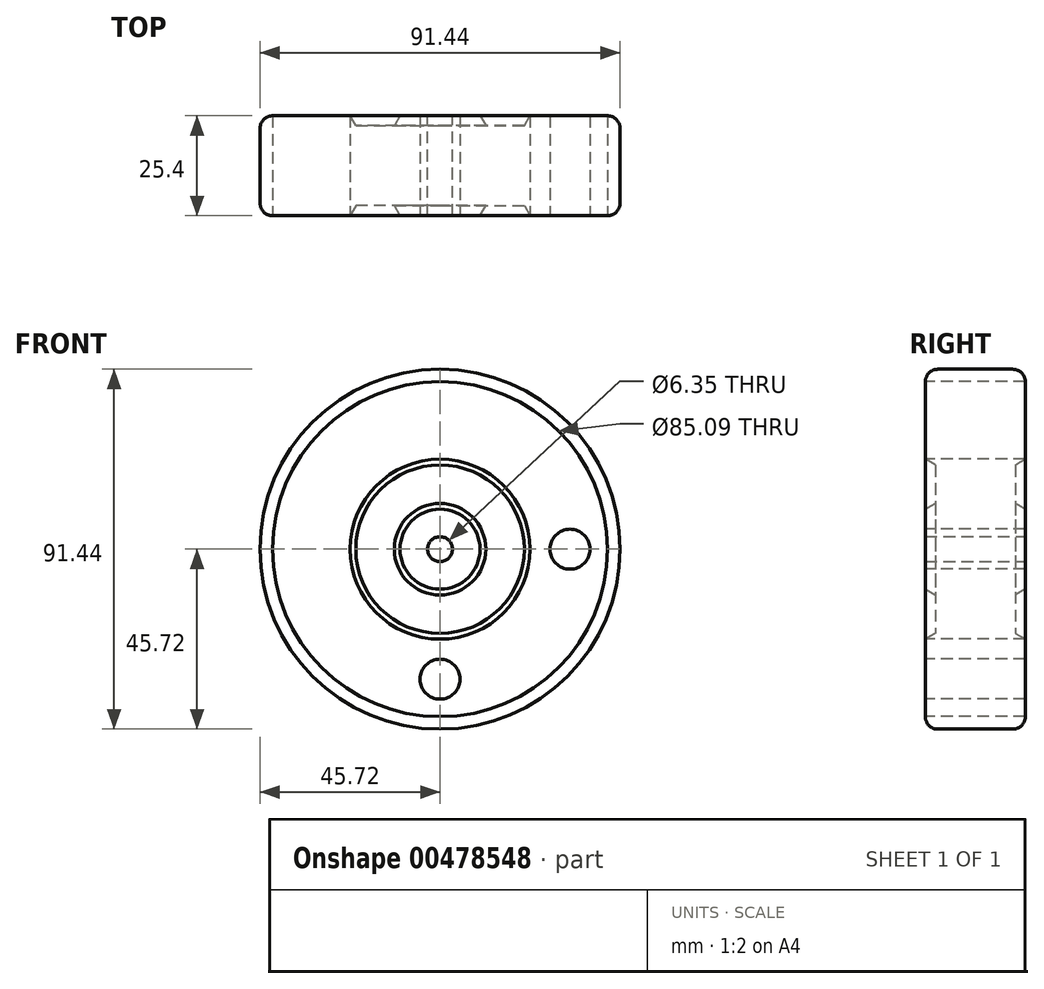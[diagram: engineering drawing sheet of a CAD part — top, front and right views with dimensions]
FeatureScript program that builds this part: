
annotation { "Feature Type Name" : "Feature", "Feature Type Description" : "" }
export const myFeature = defineFeature(function(context is Context, id is Id, definition is map)
    precondition{}
    {
        {
            var Q0;
            Q0=qCreatedBy(makeId("Right.planeOp"),FACE);
            var sketch = newSketch(context, id + "F0", { "sketchPlane" : qUnion([Q0])});
            skLineSegment(sketch, "E0", {"start": v(0, 0) * mm, "end": v(45.88, 0) * mm, "construction": true});
            skLineSegment(sketch, "E1", {"start": v(12.7, 3.18) * mm, "end": v(12.7, 10.16) * mm});
            skLineSegment(sketch, "E2", {"start": v(12.7, 10.16) * mm, "end": v(10.16, 11.63) * mm});
            skLineSegment(sketch, "E3", {"start": v(10.16, 11.63) * mm, "end": v(10.16, 21.4) * mm});
            skLineSegment(sketch, "E4", {"start": v(10.16, 21.4) * mm, "end": v(12.7, 22.86) * mm});
            skLineSegment(sketch, "E5", {"start": v(12.7, 22.86) * mm, "end": v(12.7, 42.55) * mm});
            skLineSegment(sketch, "E6.MirrorCS", {"start": v(-10.16, 21.4) * mm, "end": v(-12.7, 22.86) * mm});
            skLineSegment(sketch, "E7.MirrorCS", {"start": v(-12.7, 10.16) * mm, "end": v(-10.16, 11.63) * mm});
            skLineSegment(sketch, "E8.MirrorCS", {"start": v(-10.16, 11.63) * mm, "end": v(-10.16, 21.4) * mm});
            skLineSegment(sketch, "E9.MirrorCS", {"start": v(0, 0) * mm, "end": v(-45.88, 0) * mm, "construction": true});
            skLineSegment(sketch, "E10.MirrorCS", {"start": v(-12.7, 3.18) * mm, "end": v(-12.7, 10.16) * mm});
            skLineSegment(sketch, "E11.MirrorCS", {"start": v(-12.7, 22.86) * mm, "end": v(-12.7, 42.55) * mm});
            skLineSegment(sketch, "E12", {"start": v(-9.52, 45.72) * mm, "end": v(9.52, 45.72) * mm});
            skPoint(sketch, "E13.visualSharp", {"position": v(-12.7, 45.72) * mm});
            skArc(sketch, "E13.filletArc", {"start": v(-9.52, 45.72) * mm, "mid": v(-11.77, 44.8) * mm, "end": v(-12.7, 42.55) * mm});
            skPoint(sketch, "E14.visualSharp", {"position": v(12.7, 45.72) * mm});
            skArc(sketch, "E14.filletArc", {"start": v(12.7, 42.55) * mm, "mid": v(11.77, 44.8) * mm, "end": v(9.52, 45.72) * mm});
            skLineSegment(sketch, "E15", {"start": v(-12.7, 3.18) * mm, "end": v(12.7, 3.18) * mm});
            skSolve(sketch);
        }
        {
            var Q0;
            Q0=makeQuery(id+"F0.imprint","IMPRINT",FACE,{"disambiguationData":[TD([[makeQuery(id+"F0.imprint","IMPRINT",EDGE,{"derivedFrom":sQuery(id+"F0.wireOp",EDGE,"E1")}),1.0]])]});
            var Q1;
            Q1=sQuery(id+"F0.wireOp",EDGE,"E9.MirrorCS");
            revolve(context, id + "F1", {"entities" : qUnion([Q0]), "axis" : qUnion([Q1]), "revolveType" : RevolveType.FULL});
        }
        {
            var Q0;
            Q0=makeQuery(id+"F1.opRevolve","SWEPT_BODY",BODY,{"disambiguationData":[OSD([sQuery(id+"F0.wireOp",EDGE,"E1"),sQuery(id+"F0.wireOp",EDGE,"E2"),sQuery(id+"F0.wireOp",EDGE,"E3"),sQuery(id+"F0.wireOp",EDGE,"E4"),sQuery(id+"F0.wireOp",EDGE,"E5"),sQuery(id+"F0.wireOp",EDGE,"E6.MirrorCS"),sQuery(id+"F0.wireOp",EDGE,"E7.MirrorCS"),sQuery(id+"F0.wireOp",EDGE,"E8.MirrorCS"),sQuery(id+"F0.wireOp",EDGE,"E10.MirrorCS"),sQuery(id+"F0.wireOp",EDGE,"E11.MirrorCS"),sQuery(id+"F0.wireOp",EDGE,"E12"),sQuery(id+"F0.wireOp",EDGE,"E13.filletArc"),sQuery(id+"F0.wireOp",EDGE,"E14.filletArc"),sQuery(id+"F0.wireOp",EDGE,"E15")])]});
            transform(context, id + "F2", {"entities" : qUnion([Q0]), "transformType" : TransformType.TRANSLATION_3D, "dx" : 0 * mm, "dy" : 0 * mm, "dz" : 0 * mm, "makeCopy" : true});
        }
        {
            var Q0;
            Q0=makeQuery(id+"F1.opRevolve","SWEPT_BODY",BODY,{"disambiguationData":[OSD([sQuery(id+"F0.wireOp",EDGE,"E1"),sQuery(id+"F0.wireOp",EDGE,"E2"),sQuery(id+"F0.wireOp",EDGE,"E3"),sQuery(id+"F0.wireOp",EDGE,"E4"),sQuery(id+"F0.wireOp",EDGE,"E5"),sQuery(id+"F0.wireOp",EDGE,"E6.MirrorCS"),sQuery(id+"F0.wireOp",EDGE,"E7.MirrorCS"),sQuery(id+"F0.wireOp",EDGE,"E8.MirrorCS"),sQuery(id+"F0.wireOp",EDGE,"E10.MirrorCS"),sQuery(id+"F0.wireOp",EDGE,"E11.MirrorCS"),sQuery(id+"F0.wireOp",EDGE,"E12"),sQuery(id+"F0.wireOp",EDGE,"E13.filletArc"),sQuery(id+"F0.wireOp",EDGE,"E14.filletArc"),sQuery(id+"F0.wireOp",EDGE,"E15")])]});
            deleteBodies(context, id + "F3", {"entities" : qUnion([Q0])});
        }
        {
            var Q0;
            Q0=makeQuery(id+"F2.opPattern","COPY",FACE,{"derivedFrom":makeQuery(id+"F1.opRevolve","SWEPT_FACE",FACE,{"disambiguationData":[OSD([sQuery(id+"F0.wireOp",EDGE,"E11.MirrorCS")])]}),"instanceName":"1"});
            var sketch = newSketch(context, id + "F4", { "sketchPlane" : qUnion([Q0])});
            skCircle(sketch, "E16", {"center": v(0, 0) * mm, "radius": 33.02 * mm});
            skCircle(sketch, "E17", {"center": v(0, 33.02) * mm, "radius": 5.08 * mm});
            skCircle(sketch, "E18", {"center": v(33.02, 0) * mm, "radius": 5.08 * mm});
            skCircle(sketch, "E19", {"center": v(0, -33.02) * mm, "radius": 5.08 * mm});
            skCircle(sketch, "E20", {"center": v(-33.02, 0) * mm, "radius": 5.08 * mm});
            skSolve(sketch);
        }
        {
            var Q0;
            {var subQ0=sQuery(id+"F4.wireOp",EDGE,"E17");var subQ1=sQuery(id+"F4.wireOp",EDGE,"E16");var subQ2=makeQuery(id+"F4.imprint","INTERSECT",VERTEX,{"disambiguationData":[OD(0.0)],"derivedFrom":[subQ1,subQ0]});Q0=makeQuery(id+"F4.imprint","IMPRINT",FACE,{"disambiguationData":[TD([[makeQuery(id+"F4.imprint","IMPRINT",EDGE,{"disambiguationData":[TD([[subQ2,-1.0]])],"derivedFrom":subQ1}),1.0]])]});}
            var Q1;
            {var subQ0=sQuery(id+"F4.wireOp",EDGE,"E17");var subQ1=sQuery(id+"F4.wireOp",EDGE,"E16");var subQ2=makeQuery(id+"F4.imprint","INTERSECT",VERTEX,{"disambiguationData":[OD(0.0)],"derivedFrom":[subQ1,subQ0]});Q1=makeQuery(id+"F4.imprint","IMPRINT",FACE,{"disambiguationData":[TD([[makeQuery(id+"F4.imprint","IMPRINT",EDGE,{"disambiguationData":[TD([[subQ2,-1.0]])],"derivedFrom":subQ1}),-1.0]])]});}
            var Q2;
            {var subQ0=sQuery(id+"F4.wireOp",EDGE,"E18");var subQ1=sQuery(id+"F4.wireOp",EDGE,"E16");var subQ2=makeQuery(id+"F4.imprint","INTERSECT",VERTEX,{"disambiguationData":[OD(0.0)],"derivedFrom":[subQ1,subQ0]});Q2=makeQuery(id+"F4.imprint","IMPRINT",FACE,{"disambiguationData":[TD([[makeQuery(id+"F4.imprint","IMPRINT",EDGE,{"disambiguationData":[TD([[subQ2,1.0]])],"derivedFrom":subQ1}),1.0]])]});}
            var Q3;
            {var subQ0=sQuery(id+"F4.wireOp",EDGE,"E18");var subQ1=sQuery(id+"F4.wireOp",EDGE,"E16");var subQ2=makeQuery(id+"F4.imprint","INTERSECT",VERTEX,{"disambiguationData":[OD(0.0)],"derivedFrom":[subQ1,subQ0]});Q3=makeQuery(id+"F4.imprint","IMPRINT",FACE,{"disambiguationData":[TD([[makeQuery(id+"F4.imprint","IMPRINT",EDGE,{"disambiguationData":[TD([[subQ2,1.0]])],"derivedFrom":subQ1}),-1.0]])]});}
            var Q4;
            {var subQ0=sQuery(id+"F4.wireOp",EDGE,"E19");var subQ1=sQuery(id+"F4.wireOp",EDGE,"E16");var subQ2=makeQuery(id+"F4.imprint","INTERSECT",VERTEX,{"disambiguationData":[OD(0.0)],"derivedFrom":[subQ1,subQ0]});Q4=makeQuery(id+"F4.imprint","IMPRINT",FACE,{"disambiguationData":[TD([[makeQuery(id+"F4.imprint","IMPRINT",EDGE,{"disambiguationData":[TD([[subQ2,-1.0]])],"derivedFrom":subQ1}),1.0]])]});}
            var Q5;
            {var subQ0=sQuery(id+"F4.wireOp",EDGE,"E19");var subQ1=sQuery(id+"F4.wireOp",EDGE,"E16");var subQ2=makeQuery(id+"F4.imprint","INTERSECT",VERTEX,{"disambiguationData":[OD(0.0)],"derivedFrom":[subQ1,subQ0]});Q5=makeQuery(id+"F4.imprint","IMPRINT",FACE,{"disambiguationData":[TD([[makeQuery(id+"F4.imprint","IMPRINT",EDGE,{"disambiguationData":[TD([[subQ2,-1.0]])],"derivedFrom":subQ1}),-1.0]])]});}
            var Q6;
            {var subQ0=sQuery(id+"F4.wireOp",EDGE,"E20");var subQ1=sQuery(id+"F4.wireOp",EDGE,"E16");var subQ2=makeQuery(id+"F4.imprint","INTERSECT",VERTEX,{"disambiguationData":[OD(0.0)],"derivedFrom":[subQ1,subQ0]});Q6=makeQuery(id+"F4.imprint","IMPRINT",FACE,{"disambiguationData":[TD([[makeQuery(id+"F4.imprint","IMPRINT",EDGE,{"disambiguationData":[TD([[subQ2,-1.0]])],"derivedFrom":subQ1}),1.0]])]});}
            var Q7;
            {var subQ0=sQuery(id+"F4.wireOp",EDGE,"E20");var subQ1=sQuery(id+"F4.wireOp",EDGE,"E16");var subQ2=makeQuery(id+"F4.imprint","INTERSECT",VERTEX,{"disambiguationData":[OD(0.0)],"derivedFrom":[subQ1,subQ0]});Q7=makeQuery(id+"F4.imprint","IMPRINT",FACE,{"disambiguationData":[TD([[makeQuery(id+"F4.imprint","IMPRINT",EDGE,{"disambiguationData":[TD([[subQ2,-1.0]])],"derivedFrom":subQ1}),-1.0]])]});}
            var Q8;
            Q8=sQuery(id+"F4.wireOp",EDGE,"E17");
            var Q9;
            Q9=sQuery(id+"F4.wireOp",EDGE,"E20");
            var Q10;
            Q10=sQuery(id+"F4.wireOp",EDGE,"E19");
            var Q11;
            Q11=sQuery(id+"F4.wireOp",EDGE,"E18");
            extrude(context, id + "F5", {"entities" : qUnion([Q0, Q1, Q2, Q3, Q4, Q5, Q6, Q7]), "operationType" : NewBodyOperationType.REMOVE, "surfaceEntities" : qUnion([Q8, Q9, Q10, Q11]), "endBound" : BoundingType.THROUGH_ALL, "oppositeDirection" : true, "depth" : 25.4 * mm, "hasSecondDirection" : true, "secondDirectionOppositeDirection" : false, "secondDirectionDepth" : 25.4 * mm});
        }
    });
